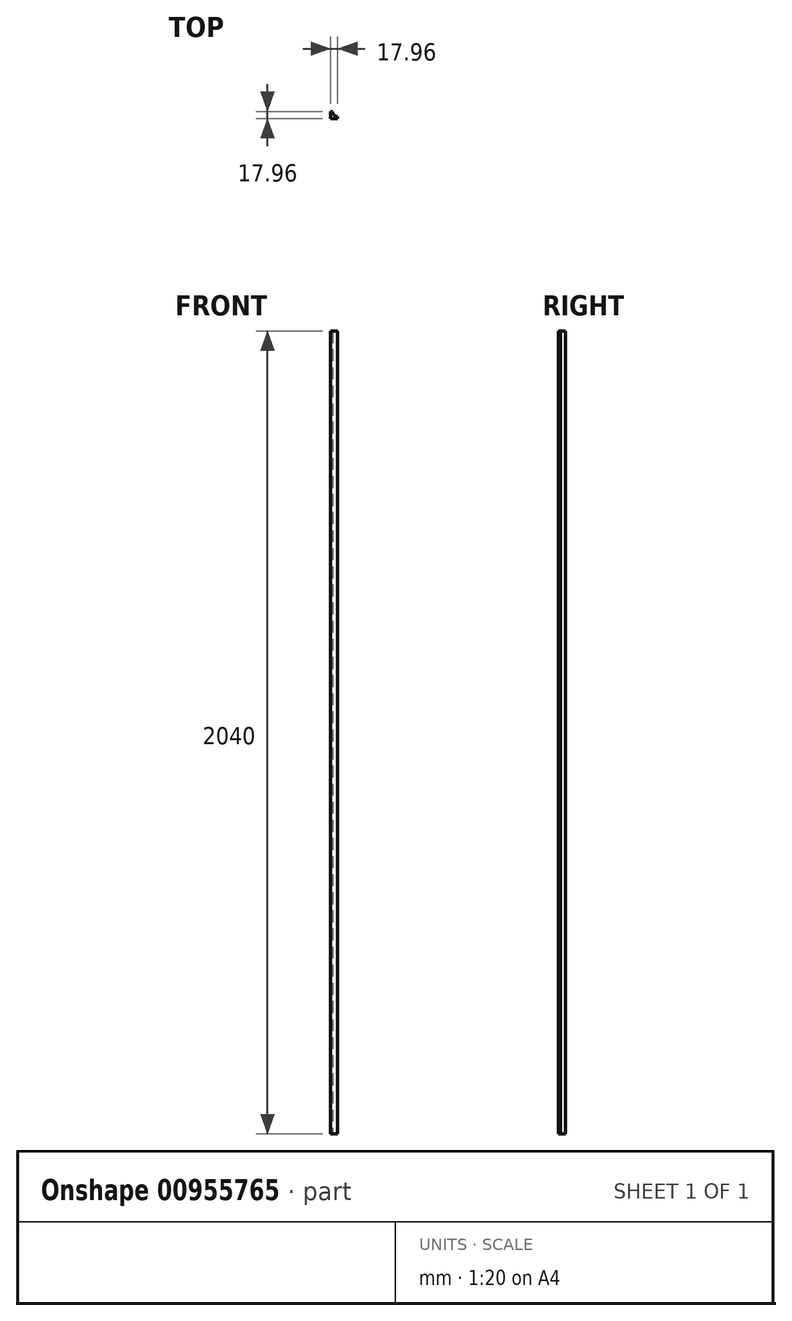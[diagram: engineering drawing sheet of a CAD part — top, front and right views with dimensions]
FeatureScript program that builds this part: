
annotation { "Feature Type Name" : "Feature", "Feature Type Description" : "" }
export const myFeature = defineFeature(function(context is Context, id is Id, definition is map)
    precondition{}
    {
        {
            var Q0;
            Q0=qCreatedBy(makeId("Top.planeOp"),FACE);
            var sketch = newSketch(context, id + "F0", { "sketchPlane" : qUnion([Q0])});
            skLineSegment(sketch, "E0.bottom", {"start": v(-58.82, -14.09) * mm, "end": v(-76.78, -14.09) * mm});
            skLineSegment(sketch, "E0.top", {"start": v(-58.82, 3.87) * mm, "end": v(-76.78, 3.87) * mm});
            skLineSegment(sketch, "E0.left", {"start": v(-58.82, -14.09) * mm, "end": v(-58.82, 3.87) * mm});
            skLineSegment(sketch, "E0.right", {"start": v(-76.78, -14.09) * mm, "end": v(-76.78, 3.87) * mm});
            skPoint(sketch, "E0.middle", {"position": v(-67.8, -5.1) * mm});
            skCircle(sketch, "E1", {"center": v(-58.82, 3.87) * mm, "radius": 12.7 * mm});
            skSolve(sketch);
        }
        {
            var Q0;
            {var subQ1=sQuery(id+"F0.wireOp",EDGE,"E0.bottom");Q0=makeQuery(id+"F0.imprint","IMPRINT",FACE,{"disambiguationData":[TD([[makeQuery(id+"F0.imprint","IMPRINT",EDGE,{"derivedFrom":subQ1}),-1.0]])]});}
            extrude(context, id + "F1", {"entities" : qUnion([Q0]), "depth" : 2040 * mm, "offsetDistance" : 25.4 * mm});
        }
    });
